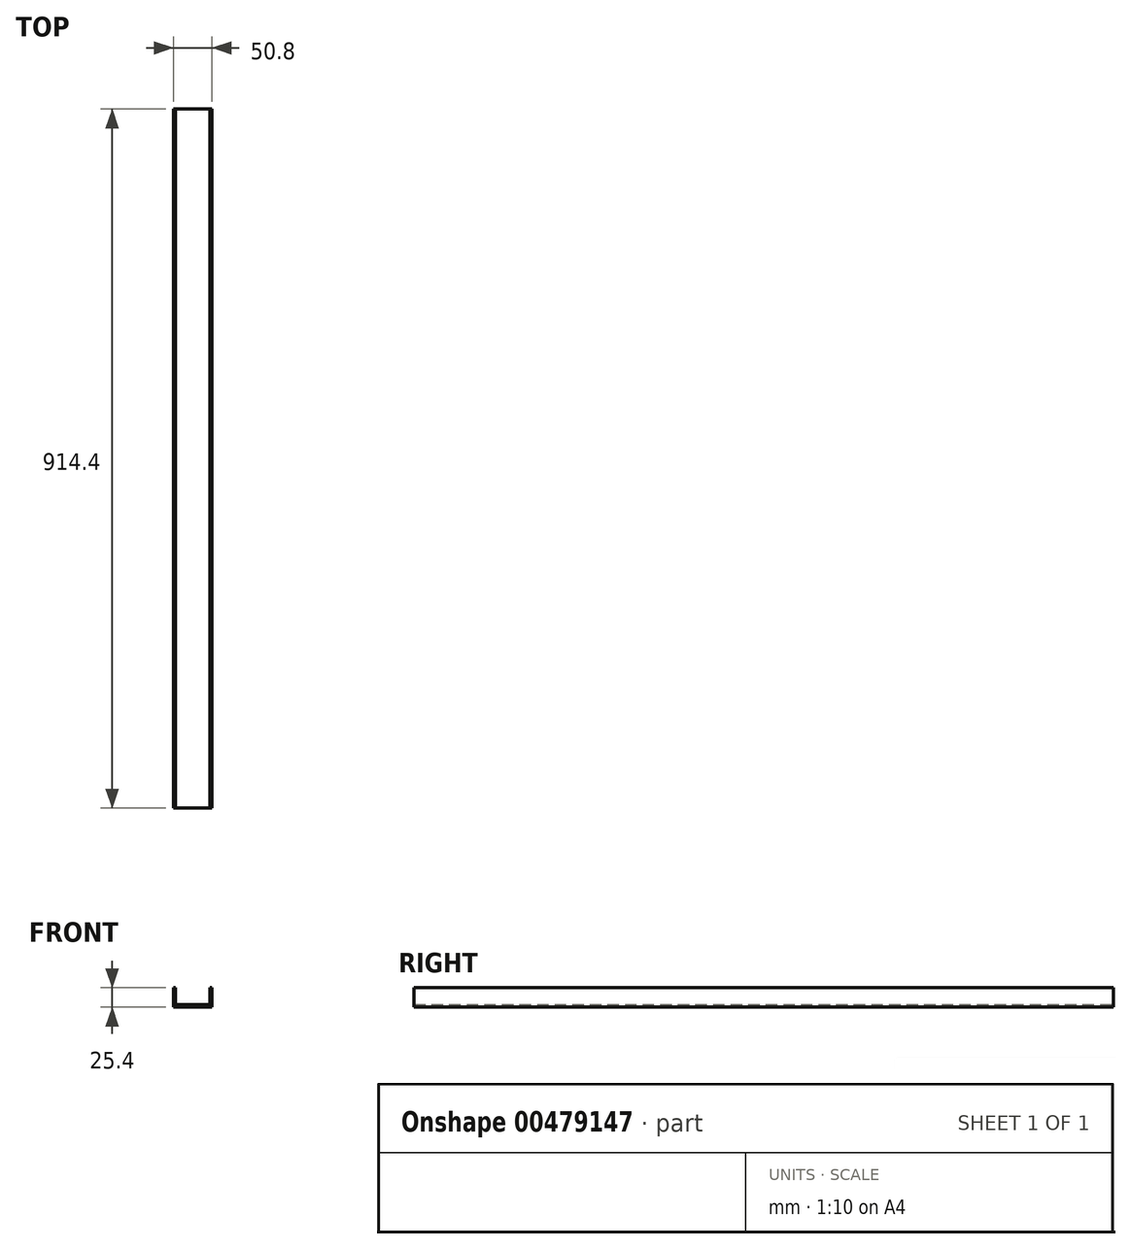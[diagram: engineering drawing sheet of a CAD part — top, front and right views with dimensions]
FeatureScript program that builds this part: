
annotation { "Feature Type Name" : "Feature", "Feature Type Description" : "" }
export const myFeature = defineFeature(function(context is Context, id is Id, definition is map)
    precondition{}
    {
        {
            var Q0;
            Q0=qCreatedBy(makeId("Front.planeOp"),FACE);
            var sketch = newSketch(context, id + "F0", { "sketchPlane" : qUnion([Q0])});
            skLineSegment(sketch, "E0", {"start": v(-44.36, 22.86) * mm, "end": v(-44.36, -2.54) * mm});
            skLineSegment(sketch, "E1", {"start": v(-44.36, -2.54) * mm, "end": v(6.44, -2.54) * mm});
            skLineSegment(sketch, "E2", {"start": v(6.44, -2.54) * mm, "end": v(6.44, 22.86) * mm});
            skLineSegment(sketch, "E3", {"start": v(6.44, 22.86) * mm, "end": v(3.27, 22.86) * mm});
            skLineSegment(sketch, "E4", {"start": v(3.27, 22.86) * mm, "end": v(3.27, 0.63) * mm});
            skLineSegment(sketch, "E5", {"start": v(3.27, 0.63) * mm, "end": v(-41.18, 0.63) * mm});
            skLineSegment(sketch, "E6", {"start": v(-41.18, 0.63) * mm, "end": v(-41.18, 22.86) * mm});
            skLineSegment(sketch, "E7", {"start": v(-41.18, 22.86) * mm, "end": v(-44.36, 22.86) * mm});
            skSolve(sketch);
        }
        {
            var Q0;
            Q0 = qSketchRegion(id + "F0", true);
            extrude(context, id + "F1", {"entities" : qUnion([Q0]), "depth" : 914.4 * mm});
        }
    });
